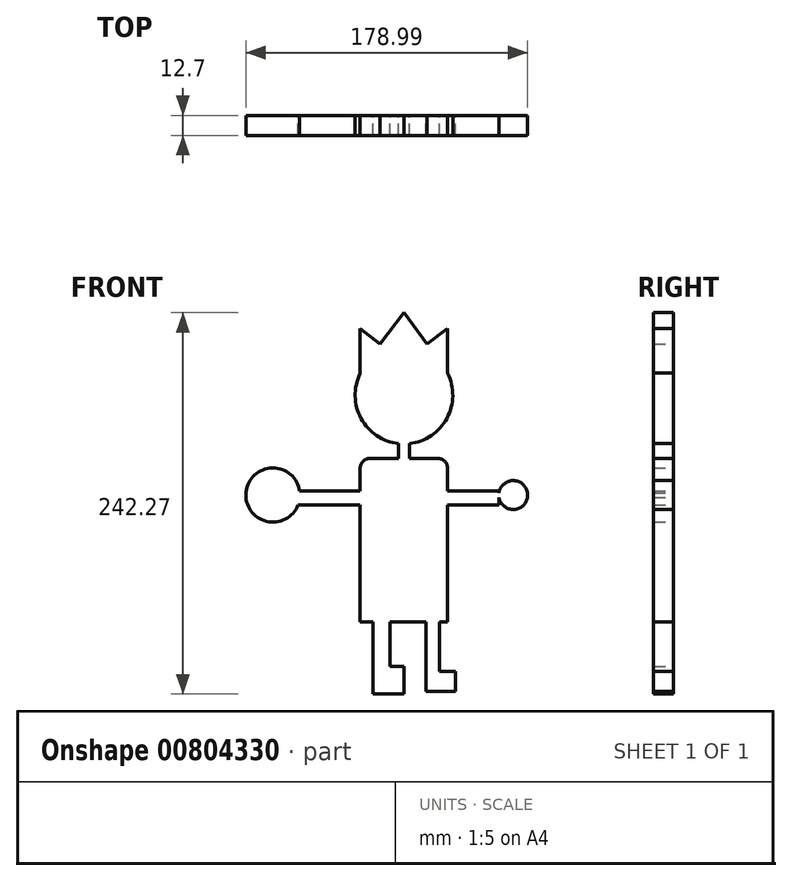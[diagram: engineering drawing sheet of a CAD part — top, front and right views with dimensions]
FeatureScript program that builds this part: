
annotation { "Feature Type Name" : "Feature", "Feature Type Description" : "" }
export const myFeature = defineFeature(function(context is Context, id is Id, definition is map)
    precondition{}
    {
        {
            var Q0;
            Q0=qCreatedBy(makeId("Front.planeOp"),FACE);
            var sketch = newSketch(context, id + "F0", { "sketchPlane" : qUnion([Q0])});
            skCircle(sketch, "E0", {"center": v(0, 0) * mm, "radius": 31 * mm});
            skLineSegment(sketch, "E1", {"start": v(-27.82, 13.69) * mm, "end": v(-27.82, 42.27) * mm});
            skLineSegment(sketch, "E2", {"start": v(-27.82, 42.27) * mm, "end": v(-15.26, 32.6) * mm});
            skLineSegment(sketch, "E3", {"start": v(-15.26, 32.6) * mm, "end": v(0, 52.4) * mm});
            skLineSegment(sketch, "E4", {"start": v(0, 52.4) * mm, "end": v(14.54, 32.6) * mm});
            skLineSegment(sketch, "E5", {"start": v(14.54, 32.6) * mm, "end": v(27.72, 42.27) * mm});
            skLineSegment(sketch, "E6", {"start": v(27.72, 42.27) * mm, "end": v(27.72, 13.69) * mm});
            skPoint(sketch, "E7.center.orphan", {"position": v(-14.78, 9.86) * mm});
            skPoint(sketch, "E8.center.orphan", {"position": v(14.73, 9.86) * mm});
            skLineSegment(sketch, "E9", {"start": v(-3.49, -30.8) * mm, "end": v(-3.49, -40.16) * mm});
            skLineSegment(sketch, "E10", {"start": v(-3.49, -40.16) * mm, "end": v(3.51, -40.16) * mm});
            skLineSegment(sketch, "E11", {"start": v(3.51, -40.16) * mm, "end": v(3.51, -30.8) * mm});
            skLineSegment(sketch, "E12", {"start": v(3.51, -40.16) * mm, "end": v(21.37, -40.16) * mm});
            skLineSegment(sketch, "E13", {"start": v(27.72, -46.5) * mm, "end": v(27.72, -75.55) * mm});
            skLineSegment(sketch, "E14", {"start": v(-3.49, -40.16) * mm, "end": v(-21.47, -40.16) * mm});
            skLineSegment(sketch, "E15", {"start": v(-27.82, -46.5) * mm, "end": v(-27.82, -75.55) * mm});
            skLineSegment(sketch, "E16", {"start": v(-27.82, -75.55) * mm, "end": v(-27.82, -100.15) * mm});
            skLineSegment(sketch, "E17", {"start": v(-27.82, -100.15) * mm, "end": v(27.72, -100.15) * mm});
            skLineSegment(sketch, "E18", {"start": v(27.72, -100.15) * mm, "end": v(27.72, -75.55) * mm});
            skPoint(sketch, "E19.visualSharp", {"position": v(-27.82, -40.16) * mm});
            skArc(sketch, "E19.filletArc", {"start": v(-21.47, -40.16) * mm, "mid": v(-25.96, -42.02) * mm, "end": v(-27.82, -46.5) * mm});
            skPoint(sketch, "E20.visualSharp", {"position": v(27.72, -40.16) * mm});
            skArc(sketch, "E20.filletArc", {"start": v(27.72, -46.5) * mm, "mid": v(25.86, -42.02) * mm, "end": v(21.37, -40.16) * mm});
            skLineSegment(sketch, "E21", {"start": v(-27.82, -100.15) * mm, "end": v(-27.82, -144.15) * mm});
            skLineSegment(sketch, "E22", {"start": v(-27.82, -144.15) * mm, "end": v(0, -144.15) * mm});
            skLineSegment(sketch, "E23", {"start": v(0, -144.15) * mm, "end": v(0, -100.15) * mm});
            skLineSegment(sketch, "E24", {"start": v(0, -100.15) * mm, "end": v(0, -144.15) * mm});
            skLineSegment(sketch, "E25", {"start": v(27.72, -144.15) * mm, "end": v(0, -144.15) * mm});
            skLineSegment(sketch, "E26", {"start": v(27.72, -144.15) * mm, "end": v(27.72, -100.15) * mm});
            skLineSegment(sketch, "E27", {"start": v(-19.55, -144.15) * mm, "end": v(-19.55, -172.4) * mm});
            skLineSegment(sketch, "E28", {"start": v(-19.55, -172.4) * mm, "end": v(-8.9, -172.4) * mm});
            skLineSegment(sketch, "E29", {"start": v(-8.9, -172.4) * mm, "end": v(-8.9, -144.15) * mm});
            skLineSegment(sketch, "E30", {"start": v(13.86, -144.15) * mm, "end": v(13.86, -175.54) * mm});
            skLineSegment(sketch, "E31", {"start": v(13.86, -175.54) * mm, "end": v(22.43, -175.54) * mm});
            skLineSegment(sketch, "E32", {"start": v(22.43, -175.54) * mm, "end": v(22.43, -144.15) * mm});
            skLineSegment(sketch, "E33.bottom", {"start": v(-19.55, -172.4) * mm, "end": v(0, -172.4) * mm});
            skLineSegment(sketch, "E33.top", {"start": v(-19.55, -189.87) * mm, "end": v(0, -189.87) * mm});
            skLineSegment(sketch, "E33.left", {"start": v(-19.55, -172.4) * mm, "end": v(-19.55, -189.87) * mm});
            skLineSegment(sketch, "E33.right", {"start": v(0, -172.4) * mm, "end": v(0, -189.87) * mm});
            skLineSegment(sketch, "E34.bottom", {"start": v(13.86, -175.54) * mm, "end": v(32.79, -175.54) * mm});
            skLineSegment(sketch, "E34.top", {"start": v(13.86, -188.09) * mm, "end": v(32.79, -188.09) * mm});
            skLineSegment(sketch, "E34.left", {"start": v(13.86, -175.54) * mm, "end": v(13.86, -188.09) * mm});
            skLineSegment(sketch, "E34.right", {"start": v(32.79, -175.54) * mm, "end": v(32.79, -188.09) * mm});
            skLineSegment(sketch, "E35", {"start": v(-27.82, -61.03) * mm, "end": v(-67.18, -61.03) * mm});
            skLineSegment(sketch, "E36", {"start": v(-67.18, -61.03) * mm, "end": v(-67.18, -69.75) * mm});
            skLineSegment(sketch, "E37", {"start": v(-67.18, -69.75) * mm, "end": v(-27.82, -69.75) * mm});
            skLineSegment(sketch, "E38", {"start": v(27.72, -61.03) * mm, "end": v(60.35, -61.03) * mm});
            skLineSegment(sketch, "E39", {"start": v(60.35, -61.03) * mm, "end": v(60.35, -69.75) * mm});
            skLineSegment(sketch, "E40", {"start": v(60.35, -69.75) * mm, "end": v(27.72, -69.75) * mm});
            skCircle(sketch, "E41", {"center": v(69.4, -63.48) * mm, "radius": 9.17 * mm});
            skCircle(sketch, "E42", {"center": v(-83.21, -63.48) * mm, "radius": 17.21 * mm});
            skSolve(sketch);
        }
        {
            var Q0;
            Q0 = qSketchRegion(id + "F0", true);
            extrude(context, id + "F1", {"entities" : qUnion([Q0]), "depth" : 12.7 * mm, "offsetDistance" : 25.4 * mm});
        }
    });
